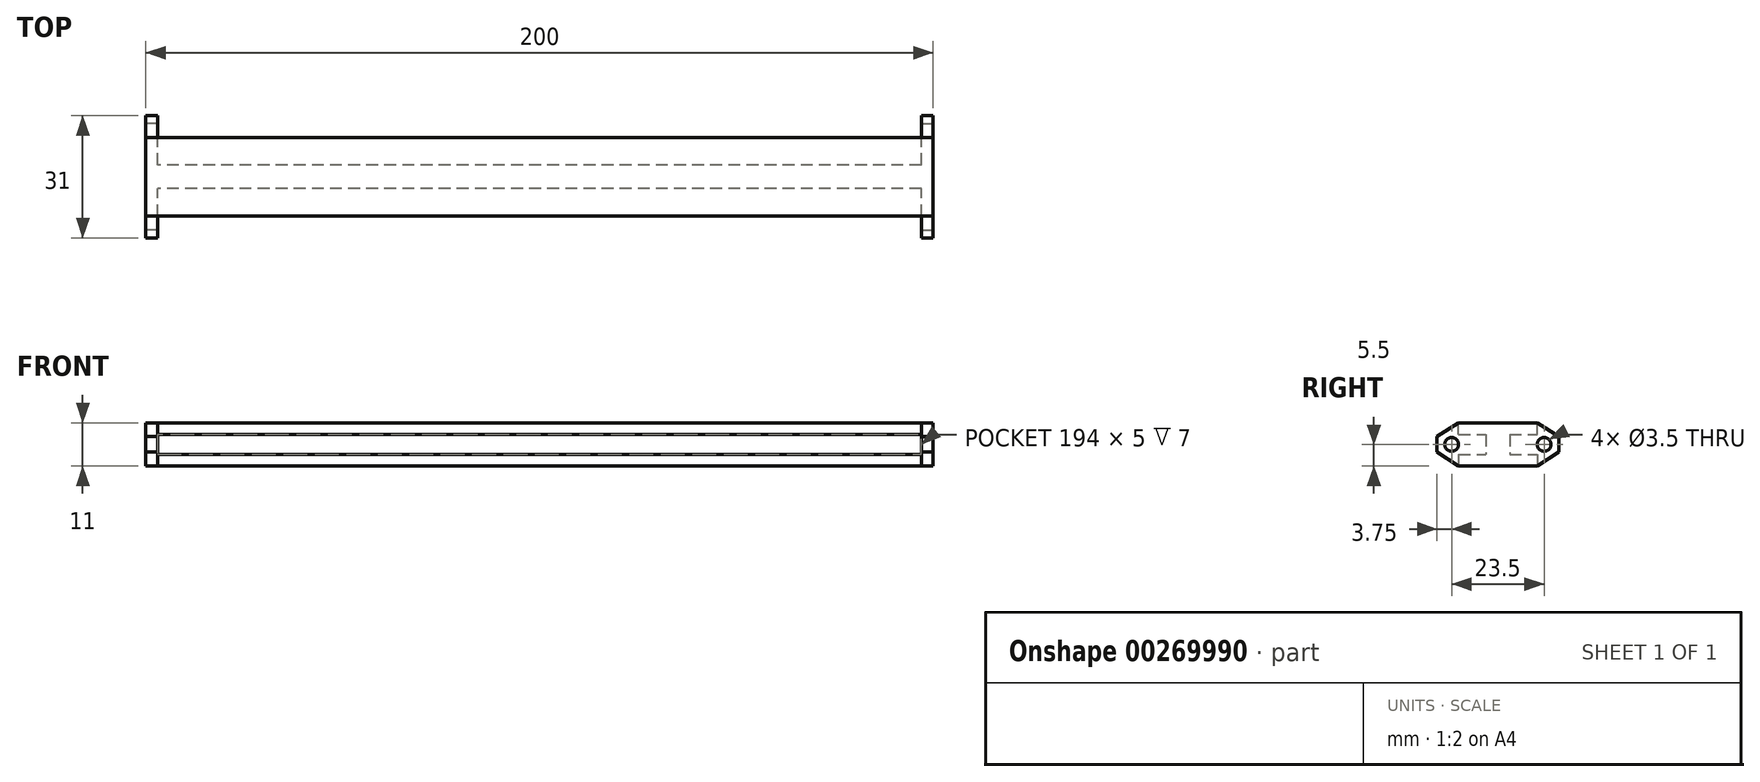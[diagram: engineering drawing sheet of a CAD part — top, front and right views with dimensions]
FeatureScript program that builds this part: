
annotation { "Feature Type Name" : "Feature", "Feature Type Description" : "" }
export const myFeature = defineFeature(function(context is Context, id is Id, definition is map)
    precondition{}
    {
        {
            var Q0;
            Q0=qCreatedBy(makeId("Right.planeOp"),FACE);
            var sketch = newSketch(context, id + "F0", { "sketchPlane" : qUnion([Q0])});
            skLineSegment(sketch, "E0.bottom", {"start": v(-10, 2.5) * mm, "end": v(-3, 2.5) * mm});
            skLineSegment(sketch, "E0.top", {"start": v(-10, 5.5) * mm, "end": v(10, 5.5) * mm});
            skLineSegment(sketch, "E0.left", {"start": v(-10, 2.5) * mm, "end": v(-10, 5.5) * mm});
            skLineSegment(sketch, "E0.right", {"start": v(10, 2.5) * mm, "end": v(10, 5.5) * mm});
            skLineSegment(sketch, "E1.left", {"start": v(-3, 2.5) * mm, "end": v(-3, -2.5) * mm});
            skLineSegment(sketch, "E1.right", {"start": v(3, 2.5) * mm, "end": v(3, -2.5) * mm});
            skPoint(sketch, "E2.firstSnap0", {"position": v(-10, 4) * mm});
            skLineSegment(sketch, "E2.bottom", {"start": v(-10, -2.5) * mm, "end": v(-3, -2.5) * mm});
            skLineSegment(sketch, "E2.top", {"start": v(-10, -5.5) * mm, "end": v(10, -5.5) * mm});
            skLineSegment(sketch, "E2.left", {"start": v(-10, -2.5) * mm, "end": v(-10, -5.5) * mm});
            skLineSegment(sketch, "E2.right", {"start": v(10, -2.5) * mm, "end": v(10, -5.5) * mm});
            skLineSegment(sketch, "E3.trimOffspring", {"start": v(3, -2.5) * mm, "end": v(10, -2.5) * mm});
            skLineSegment(sketch, "E4.trimOffspring", {"start": v(3, 2.5) * mm, "end": v(10, 2.5) * mm});
            skLineSegment(sketch, "E5", {"start": v(-10, 5.5) * mm, "end": v(-15.5, 2.03) * mm});
            skLineSegment(sketch, "E6", {"start": v(-15.5, 2.03) * mm, "end": v(-15.5, -1.97) * mm});
            skLineSegment(sketch, "E7", {"start": v(-15.5, -1.97) * mm, "end": v(-10, -5.5) * mm});
            skCircle(sketch, "E8", {"center": v(-11.75, 0) * mm, "radius": 1.75 * mm});
            skPoint(sketch, "E9", {"position": v(-11.75, 1.75) * mm});
            skPoint(sketch, "E10", {"position": v(-13.5, 0) * mm});
            skPoint(sketch, "E11", {"position": v(0, 5.5) * mm});
            skPoint(sketch, "E12", {"position": v(3, 0) * mm});
            skLineSegment(sketch, "E13", {"start": v(0, 5.5) * mm, "end": v(0, -5.5) * mm, "construction": true});
            skLineSegment(sketch, "E14.MirrorCS", {"start": v(10, 5.5) * mm, "end": v(15.5, 2.03) * mm});
            skLineSegment(sketch, "E15.MirrorCS", {"start": v(15.5, 2.03) * mm, "end": v(15.5, -1.97) * mm});
            skLineSegment(sketch, "E16.MirrorCS", {"start": v(15.5, -1.97) * mm, "end": v(10, -5.5) * mm});
            skCircle(sketch, "E17.MirrorC", {"center": v(11.75, 0) * mm, "radius": 1.75 * mm});
            skLineSegment(sketch, "E18", {"start": v(-10, 2.5) * mm, "end": v(-10, -2.5) * mm, "construction": true});
            skPoint(sketch, "E19", {"position": v(0, 0) * mm});
            skSolve(sketch);
        }
        {
            var Q0;
            Q0=makeQuery(id+"F0.imprint","IMPRINT",FACE,{"disambiguationData":[TD([[makeQuery(id+"F0.imprint","IMPRINT",EDGE,{"derivedFrom":sQuery(id+"F0.wireOp",EDGE,"E0.bottom")}),-1.0]])]});
            var Q1;
            Q1=makeQuery(id+"F0.imprint","IMPRINT",FACE,{"disambiguationData":[TD([[makeQuery(id+"F0.imprint","IMPRINT",EDGE,{"derivedFrom":sQuery(id+"F0.wireOp",EDGE,"E0.right")}),-1.0]])]});
            extrude(context, id + "F1", {"entities" : qUnion([Q0, Q1]), "depth" : 3 * mm, "offsetDistance" : 25 * mm});
        }
        {
            var Q0;
            Q0=makeQuery(id+"F0.imprint","IMPRINT",FACE,{"disambiguationData":[TD([[makeQuery(id+"F0.imprint","IMPRINT",EDGE,{"derivedFrom":sQuery(id+"F0.wireOp",EDGE,"E0.bottom")}),1.0]])]});
            extrude(context, id + "F2", {"entities" : qUnion([Q0]), "operationType" : NewBodyOperationType.ADD, "depth" : 200 * mm, "offsetDistance" : 25 * mm});
        }
        {
            var Q0;
            Q0=makeQuery(id+"F2.opExtrude","CAP_FACE",FACE,{"disambiguationData":[OSD([sQuery(id+"F0.wireOp",EDGE,"E0.bottom"),sQuery(id+"F0.wireOp",EDGE,"E0.top"),sQuery(id+"F0.wireOp",EDGE,"E0.left"),sQuery(id+"F0.wireOp",EDGE,"E0.right"),sQuery(id+"F0.wireOp",EDGE,"E1.left"),sQuery(id+"F0.wireOp",EDGE,"E1.right"),sQuery(id+"F0.wireOp",EDGE,"E2.bottom"),sQuery(id+"F0.wireOp",EDGE,"E2.top"),sQuery(id+"F0.wireOp",EDGE,"E2.left"),sQuery(id+"F0.wireOp",EDGE,"E2.right"),sQuery(id+"F0.wireOp",EDGE,"E3.trimOffspring"),sQuery(id+"F0.wireOp",EDGE,"E4.trimOffspring")])],"isStart":false});
            var sketch = newSketch(context, id + "F3", { "sketchPlane" : qUnion([Q0])});
            skLineSegment(sketch, "E20.bottom", {"start": v(-10, 2.5) * mm, "end": v(-3, 2.5) * mm});
            skLineSegment(sketch, "E20.top", {"start": v(-10, 5.5) * mm, "end": v(10, 5.5) * mm});
            skLineSegment(sketch, "E20.left", {"start": v(-10, 2.5) * mm, "end": v(-10, 5.5) * mm});
            skLineSegment(sketch, "E20.right", {"start": v(10, 2.5) * mm, "end": v(10, 5.5) * mm});
            skLineSegment(sketch, "E21.left", {"start": v(-3, 2.5) * mm, "end": v(-3, -2.5) * mm});
            skLineSegment(sketch, "E21.right", {"start": v(3, 2.5) * mm, "end": v(3, -2.5) * mm});
            skPoint(sketch, "E22.firstSnap0", {"position": v(-10, 4) * mm});
            skLineSegment(sketch, "E22.bottom", {"start": v(-10, -2.5) * mm, "end": v(-3, -2.5) * mm});
            skLineSegment(sketch, "E22.top", {"start": v(-10, -5.5) * mm, "end": v(10, -5.5) * mm});
            skLineSegment(sketch, "E22.left", {"start": v(-10, -2.5) * mm, "end": v(-10, -5.5) * mm});
            skLineSegment(sketch, "E22.right", {"start": v(10, -2.5) * mm, "end": v(10, -5.5) * mm});
            skLineSegment(sketch, "E23.trimOffspring", {"start": v(3, -2.5) * mm, "end": v(10, -2.5) * mm});
            skLineSegment(sketch, "E24.trimOffspring", {"start": v(3, 2.5) * mm, "end": v(10, 2.5) * mm});
            skLineSegment(sketch, "E25", {"start": v(-10, 5.5) * mm, "end": v(-15.5, 2.03) * mm});
            skLineSegment(sketch, "E26", {"start": v(-15.5, 2.03) * mm, "end": v(-15.5, -1.97) * mm});
            skLineSegment(sketch, "E27", {"start": v(-15.5, -1.97) * mm, "end": v(-10, -5.5) * mm});
            skCircle(sketch, "E28", {"center": v(-11.75, 0) * mm, "radius": 1.75 * mm});
            skPoint(sketch, "E29", {"position": v(-11.75, 1.75) * mm});
            skPoint(sketch, "E30", {"position": v(-13.5, 0) * mm});
            skPoint(sketch, "E31", {"position": v(0, 5.5) * mm});
            skPoint(sketch, "E32", {"position": v(3, 0) * mm});
            skLineSegment(sketch, "E33", {"start": v(0, 5.5) * mm, "end": v(0, -5.5) * mm, "construction": true});
            skLineSegment(sketch, "E34.MirrorCS", {"start": v(10, 5.5) * mm, "end": v(15.5, 2.03) * mm});
            skLineSegment(sketch, "E35.MirrorCS", {"start": v(15.5, 2.03) * mm, "end": v(15.5, -1.97) * mm});
            skLineSegment(sketch, "E36.MirrorCS", {"start": v(15.5, -1.97) * mm, "end": v(10, -5.5) * mm});
            skCircle(sketch, "E37.MirrorC", {"center": v(11.75, 0) * mm, "radius": 1.75 * mm});
            skLineSegment(sketch, "E38", {"start": v(-10, 2.5) * mm, "end": v(-10, -2.5) * mm, "construction": true});
            skPoint(sketch, "E39", {"position": v(0, 0) * mm});
            skSolve(sketch);
        }
        {
            var Q0;
            Q0=makeQuery(id+"F3.imprint","IMPRINT",FACE,{"disambiguationData":[TD([[makeQuery(id+"F3.imprint","IMPRINT",EDGE,{"derivedFrom":sQuery(id+"F3.wireOp",EDGE,"E20.bottom")}),-1.0]])]});
            var Q1;
            Q1=makeQuery(id+"F3.imprint","IMPRINT",FACE,{"disambiguationData":[TD([[makeQuery(id+"F3.imprint","IMPRINT",EDGE,{"derivedFrom":sQuery(id+"F3.wireOp",EDGE,"E20.right")}),-1.0]])]});
            extrude(context, id + "F4", {"entities" : qUnion([Q0, Q1]), "operationType" : NewBodyOperationType.ADD, "oppositeDirection" : true, "depth" : 3 * mm, "offsetDistance" : 25 * mm});
        }
    });
